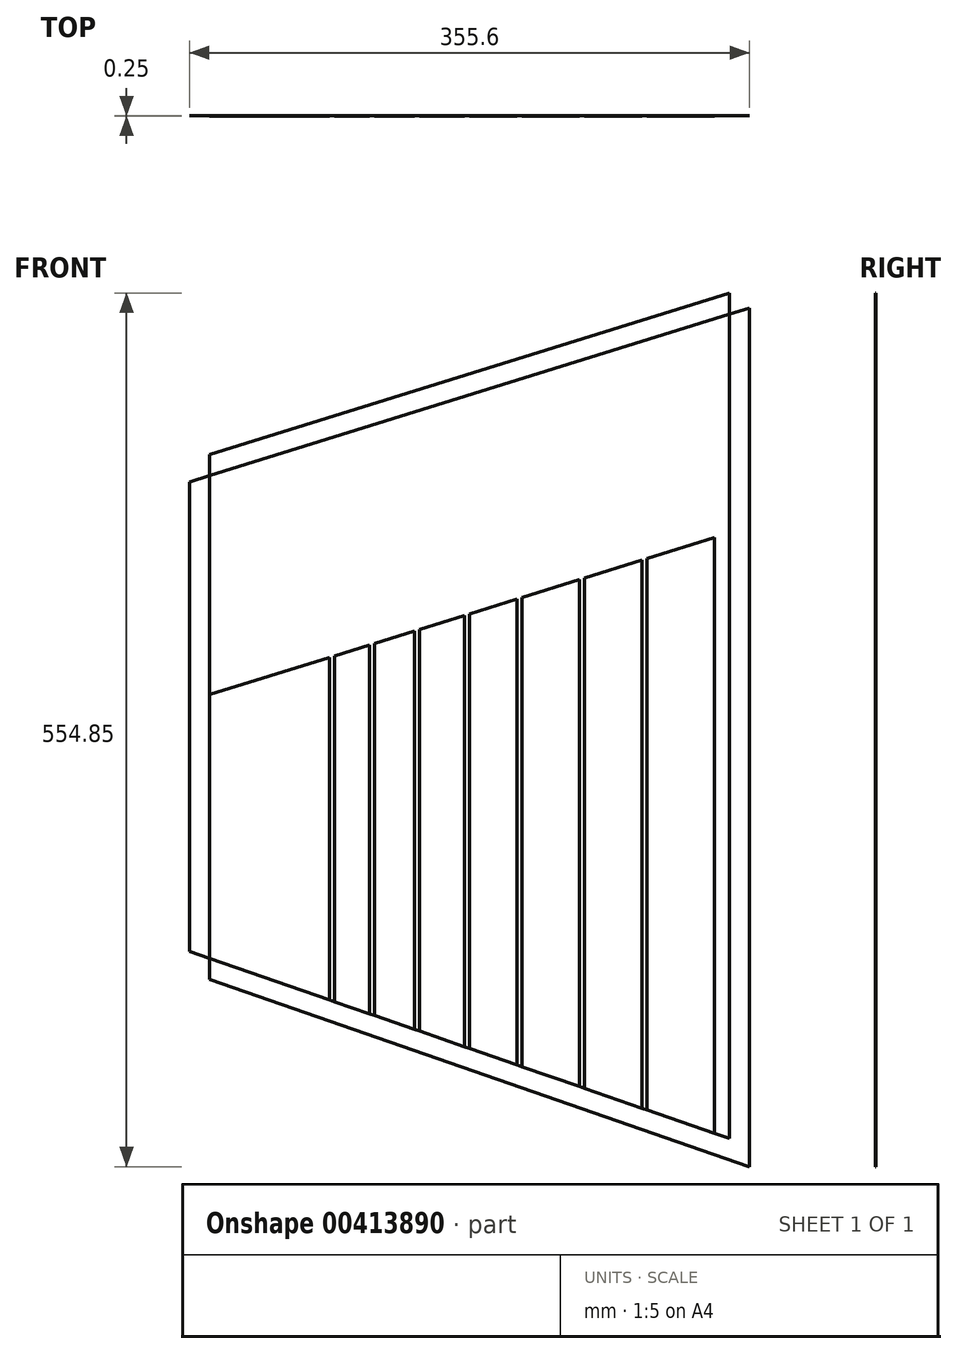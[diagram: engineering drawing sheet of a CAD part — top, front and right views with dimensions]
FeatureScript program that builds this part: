
annotation { "Feature Type Name" : "Feature", "Feature Type Description" : "" }
export const myFeature = defineFeature(function(context is Context, id is Id, definition is map)
    precondition{}
    {
        {
            var Q0;
            Q0=qCreatedBy(makeId("Front.planeOp"),FACE);
            var sketch = newSketch(context, id + "F0", { "sketchPlane" : qUnion([Q0])});
            skLineSegment(sketch, "E0", {"start": v(-177.8, 0) * mm, "end": v(177.8, 0) * mm, "construction": true});
            skLineSegment(sketch, "E1", {"start": v(-177.8, 0) * mm, "end": v(-177.8, -79.92) * mm});
            skLineSegment(sketch, "E2", {"start": v(177.8, 0) * mm, "end": v(177.8, -203.2) * mm});
            skLineSegment(sketch, "E3", {"start": v(177.8, -203.2) * mm, "end": v(-177.8, -79.92) * mm});
            skLineSegment(sketch, "E4", {"start": v(-177.8, 0) * mm, "end": v(-177.8, 245.1) * mm});
            skLineSegment(sketch, "E5", {"start": v(177.8, 0) * mm, "end": v(177.8, 355.6) * mm});
            skLineSegment(sketch, "E6", {"start": v(177.8, 355.6) * mm, "end": v(-177.8, 245.11) * mm});
            skLineSegment(sketch, "E7", {"start": v(177.8, 203.2) * mm, "end": v(-177.8, 92.7) * mm});
            skLineSegment(sketch, "E8", {"start": v(165.1, 351.65) * mm, "end": v(165.1, -198.8) * mm});
            skLineSegment(sketch, "E9", {"start": v(-165.1, 249.06) * mm, "end": v(-165.1, -84.33) * mm});
            skLineSegment(sketch, "E10", {"start": v(-177.8, -66.48) * mm, "end": v(177.8, -189.76) * mm});
            skLineSegment(sketch, "E11", {"start": v(155.57, -195.5) * mm, "end": v(155.57, 196.3) * mm});
            skLineSegment(sketch, "E12", {"start": v(112.71, 182.98) * mm, "end": v(112.71, -167.2) * mm});
            skLineSegment(sketch, "E13", {"start": v(109.54, -166.1) * mm, "end": v(109.54, 181.99) * mm});
            skLineSegment(sketch, "E14", {"start": v(30.16, 157.33) * mm, "end": v(33.34, 158.31) * mm});
            skLineSegment(sketch, "E15", {"start": v(0, -128.12) * mm, "end": v(0, 147.96) * mm});
            skPoint(sketch, "E15.endSnap0", {"position": v(0, 147.96) * mm});
            skLineSegment(sketch, "E16.trimOffspring", {"start": v(73.03, -153.44) * mm, "end": v(73.03, 170.64) * mm});
            skLineSegment(sketch, "E17.trimOffspring", {"start": v(69.85, -152.34) * mm, "end": v(69.85, 169.66) * mm});
            skLineSegment(sketch, "E18.trimOffspring", {"start": v(33.34, -139.68) * mm, "end": v(33.34, 158.31) * mm});
            skLineSegment(sketch, "E19.trimOffspring", {"start": v(30.16, -138.58) * mm, "end": v(30.16, 157.33) * mm});
            skLineSegment(sketch, "E20", {"start": v(-31.75, -117.11) * mm, "end": v(-31.75, 138.09) * mm});
            skLineSegment(sketch, "E21", {"start": v(-34.92, -116.01) * mm, "end": v(-34.93, 137.1) * mm});
            skLineSegment(sketch, "E22.trimOffspring", {"start": v(-88.9, -97.3) * mm, "end": v(-88.9, 120.33) * mm});
            skLineSegment(sketch, "E23.trimOffspring", {"start": v(-85.72, -98.4) * mm, "end": v(-85.72, 121.32) * mm});
            skLineSegment(sketch, "E24.trimOffspring", {"start": v(-63.5, -106.1) * mm, "end": v(-63.5, 128.22) * mm});
            skLineSegment(sketch, "E25.trimOffspring", {"start": v(-60.33, -107.2) * mm, "end": v(-60.33, 129.21) * mm});
            skLineSegment(sketch, "E26.trimOffspring", {"start": v(-3.17, -127.02) * mm, "end": v(-3.18, 146.97) * mm});
            skLineSegment(sketch, "E27", {"start": v(-177.8, 231.81) * mm, "end": v(177.8, 342.3) * mm});
            skLineSegment(sketch, "E28", {"start": v(158.75, 197.28) * mm, "end": v(158.75, -183.15) * mm});
            skSolve(sketch);
        }
        {
            var Q0;
            {var subQ0=sQuery(id+"F0.wireOp",EDGE,"E22.trimOffspring");Q0=makeQuery(id+"F0.imprint","IMPRINT",FACE,{"disambiguationData":[TD([[makeQuery(id+"F0.imprint","IMPRINT",EDGE,{"derivedFrom":subQ0}),1.0]])]});}
            var Q1;
            {var subQ0=sQuery(id+"F0.wireOp",EDGE,"E23.trimOffspring");Q1=makeQuery(id+"F0.imprint","IMPRINT",FACE,{"disambiguationData":[TD([[makeQuery(id+"F0.imprint","IMPRINT",EDGE,{"derivedFrom":subQ0}),-1.0]])]});}
            var Q2;
            {var subQ0=sQuery(id+"F0.wireOp",EDGE,"E21");Q2=makeQuery(id+"F0.imprint","IMPRINT",FACE,{"disambiguationData":[TD([[makeQuery(id+"F0.imprint","IMPRINT",EDGE,{"derivedFrom":subQ0}),1.0]])]});}
            var Q3;
            {var subQ0=sQuery(id+"F0.wireOp",EDGE,"E20");Q3=makeQuery(id+"F0.imprint","IMPRINT",FACE,{"disambiguationData":[TD([[makeQuery(id+"F0.imprint","IMPRINT",EDGE,{"derivedFrom":subQ0}),-1.0]])]});}
            var Q4;
            {var subQ2=sQuery(id+"F0.wireOp",EDGE,"E15");Q4=makeQuery(id+"F0.imprint","IMPRINT",FACE,{"disambiguationData":[TD([[makeQuery(id+"F0.imprint","IMPRINT",EDGE,{"derivedFrom":subQ2}),-1.0]])]});}
            var Q5;
            {var subQ2=sQuery(id+"F0.wireOp",EDGE,"E17.trimOffspring");Q5=makeQuery(id+"F0.imprint","IMPRINT",FACE,{"disambiguationData":[TD([[makeQuery(id+"F0.imprint","IMPRINT",EDGE,{"derivedFrom":subQ2}),1.0]])]});}
            var Q6;
            {var subQ3=sQuery(id+"F0.wireOp",EDGE,"E12");Q6=makeQuery(id+"F0.imprint","IMPRINT",FACE,{"disambiguationData":[TD([[makeQuery(id+"F0.imprint","IMPRINT",EDGE,{"derivedFrom":subQ3}),1.0]])]});}
            var Q7;
            {var subQ0=sQuery(id+"F0.wireOp",EDGE,"E13");Q7=makeQuery(id+"F0.imprint","IMPRINT",FACE,{"disambiguationData":[TD([[makeQuery(id+"F0.imprint","IMPRINT",EDGE,{"derivedFrom":subQ0}),1.0]])]});}
            var Q8;
            {var subQ5=sQuery(id+"F0.wireOp",EDGE,"E14");Q8=makeQuery(id+"F0.imprint","IMPRINT",FACE,{"disambiguationData":[TD([[makeQuery(id+"F0.imprint","IMPRINT",EDGE,{"derivedFrom":subQ5}),1.0]])]});}
            extrude(context, id + "F1", {"entities" : qUnion([Q0, Q1, Q2, Q3, Q4, Q5, Q6, Q7, Q8]), "depth" : 0.25 * mm});
        }
        {
            var Q0;
            {var subQ0=sQuery(id+"F0.wireOp",EDGE,"E7");var subQ1=sQuery(id+"F0.wireOp",EDGE,"E4");var subQ2=makeQuery(id+"F0.imprint","INTERSECT",VERTEX,{"derivedFrom":[subQ1,subQ0]});Q0=makeQuery(id+"F0.imprint","IMPRINT",FACE,{"disambiguationData":[TD([[makeQuery(id+"F0.imprint","IMPRINT",EDGE,{"disambiguationData":[TD([[subQ2,-1.0]])],"derivedFrom":subQ1}),-1.0]])]});}
            var Q1;
            {var subQ0=sQuery(id+"F0.wireOp",EDGE,"E8");var subQ1=sQuery(id+"F0.wireOp",EDGE,"E6");var subQ2=makeQuery(id+"F0.imprint","INTERSECT",VERTEX,{"derivedFrom":[subQ1,subQ0]});Q1=makeQuery(id+"F0.imprint","IMPRINT",FACE,{"disambiguationData":[TD([[makeQuery(id+"F0.imprint","IMPRINT",EDGE,{"disambiguationData":[TD([[subQ2,-1.0]])],"derivedFrom":subQ1}),1.0]])]});}
            var Q2;
            {var subQ0=sQuery(id+"F0.wireOp",EDGE,"E7");var subQ1=sQuery(id+"F0.wireOp",EDGE,"E5");var subQ2=makeQuery(id+"F0.imprint","INTERSECT",VERTEX,{"derivedFrom":[subQ1,subQ0]});Q2=makeQuery(id+"F0.imprint","IMPRINT",FACE,{"disambiguationData":[TD([[makeQuery(id+"F0.imprint","IMPRINT",EDGE,{"disambiguationData":[TD([[subQ2,-1.0]])],"derivedFrom":subQ1}),1.0]])]});}
            var Q3;
            {var subQ1=sQuery(id+"F0.wireOp",EDGE,"E4");var subQ5=sQuery(id+"F0.wireOp",EDGE,"E1");var subQ6=makeQuery(id+"F0.imprint","INTERSECT",VERTEX,{"derivedFrom":[subQ5,subQ1]});Q3=makeQuery(id+"F0.imprint","IMPRINT",FACE,{"disambiguationData":[TD([[makeQuery(id+"F0.imprint","IMPRINT",EDGE,{"disambiguationData":[TD([[subQ6,-1.0]])],"derivedFrom":subQ5}),1.0]])]});}
            var Q4;
            {var subQ8=sQuery(id+"F0.wireOp",EDGE,"E9");var subQ9=sQuery(id+"F0.wireOp",EDGE,"E3");var subQ10=makeQuery(id+"F0.imprint","INTERSECT",VERTEX,{"derivedFrom":[subQ9,subQ8]});Q4=makeQuery(id+"F0.imprint","IMPRINT",FACE,{"disambiguationData":[TD([[makeQuery(id+"F0.imprint","IMPRINT",EDGE,{"disambiguationData":[TD([[subQ10,1.0]])],"derivedFrom":subQ9}),-1.0]])]});}
            var Q5;
            {var subQ5=sQuery(id+"F0.wireOp",EDGE,"E5");var subQ6=sQuery(id+"F0.wireOp",EDGE,"E2");var subQ7=makeQuery(id+"F0.imprint","INTERSECT",VERTEX,{"derivedFrom":[subQ6,subQ5]});Q5=makeQuery(id+"F0.imprint","IMPRINT",FACE,{"disambiguationData":[TD([[makeQuery(id+"F0.imprint","IMPRINT",EDGE,{"disambiguationData":[TD([[subQ7,-1.0]])],"derivedFrom":subQ6}),-1.0]])]});}
            var Q6;
            {var subQ0=sQuery(id+"F0.wireOp",EDGE,"E8");var subQ1=sQuery(id+"F0.wireOp",EDGE,"E3");var subQ2=makeQuery(id+"F0.imprint","INTERSECT",VERTEX,{"derivedFrom":[subQ1,subQ0]});Q6=makeQuery(id+"F0.imprint","IMPRINT",FACE,{"disambiguationData":[TD([[makeQuery(id+"F0.imprint","IMPRINT",EDGE,{"disambiguationData":[TD([[subQ2,-1.0]])],"derivedFrom":subQ1}),-1.0]])]});}
            var Q7;
            {var subQ0=sQuery(id+"F0.wireOp",EDGE,"E3");var subQ1=sQuery(id+"F0.wireOp",EDGE,"E2");var subQ2=makeQuery(id+"F0.imprint","INTERSECT",VERTEX,{"derivedFrom":[subQ1,subQ0]});Q7=makeQuery(id+"F0.imprint","IMPRINT",FACE,{"disambiguationData":[TD([[makeQuery(id+"F0.imprint","IMPRINT",EDGE,{"disambiguationData":[TD([[subQ2,1.0]])],"derivedFrom":subQ1}),-1.0]])]});}
            extrude(context, id + "F2", {"entities" : qUnion([Q0, Q1, Q2, Q3, Q4, Q5, Q6, Q7]), "operationType" : NewBodyOperationType.ADD, "depth" : 0.13 * mm});
        }
    });
